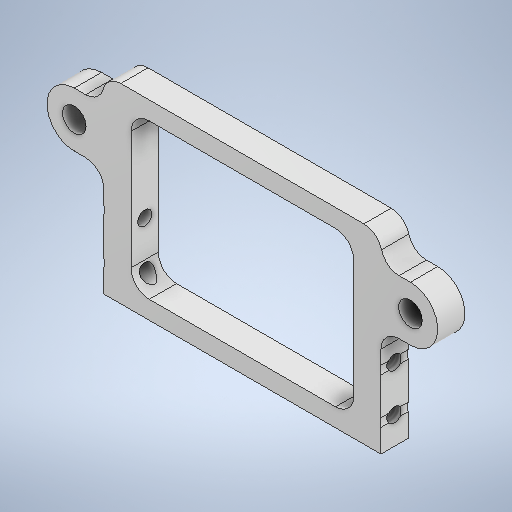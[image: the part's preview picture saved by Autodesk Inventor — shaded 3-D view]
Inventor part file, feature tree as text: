
AUTODESK INVENTOR PART (.ipt)
format: ipt  version: 2025.1 (Build 291241000, 241)  size: 356,352 bytes
history: native  units: mm
features: sketch x4, extrude x3, fillet x2, other x1, hole x1
ambient origin geometry x8: Origin, YZ Plane, XZ Plane, XY Plane, X Axis, Y Axis, Z Axis, Center Point
bodies: Body1 (feature_tree)
feature tree (11):
  other  "ソリッド1"
  extrude  "押し出し1"  Depth=2.6mm
  fillet  "フィレット1"  Radius=18.5mm
  extrude  "押し出し3"  Depth=6.0mm
  fillet  "フィレット2"  Radius=6.0mm
  hole  "穴1"  [1 undecoded]
  extrude  "押し出し2"  Depth=3.0mm
  sketch  "スケッチ1"
  sketch  "スケッチ2"
  sketch  "スケッチ3"
  sketch  "スケッチ4"
note: 1 required parameter value undecoded (feature->parameter linkage not recoverable at this tier; creation-order binding heuristic only, values carry confidence <= 0.55)
